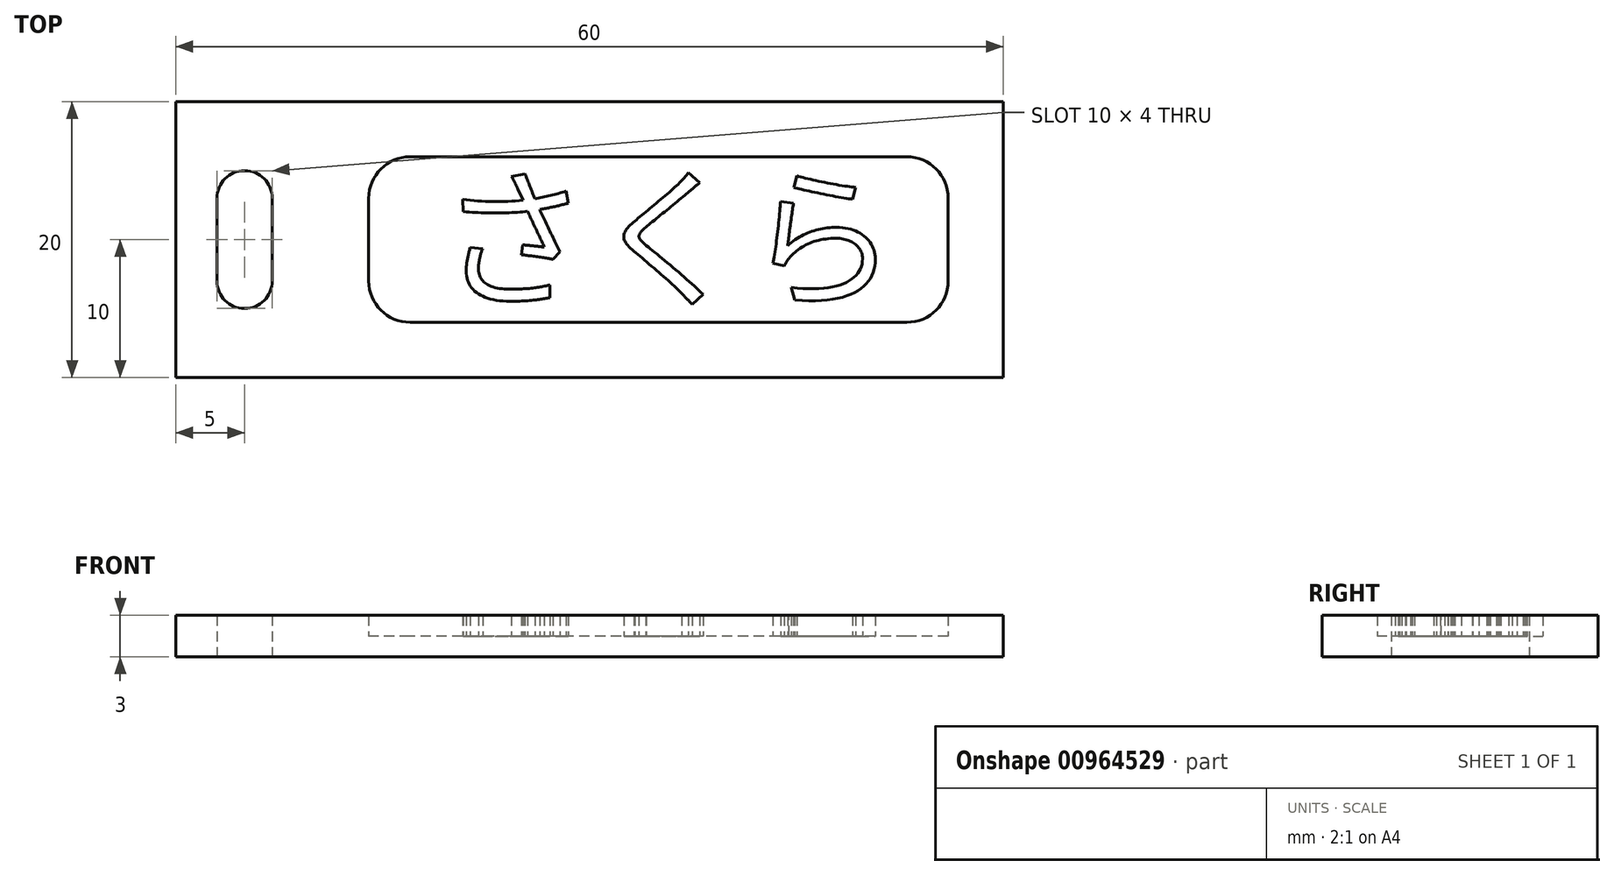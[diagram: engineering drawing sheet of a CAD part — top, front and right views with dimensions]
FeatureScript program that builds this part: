
annotation { "Feature Type Name" : "Feature", "Feature Type Description" : "" }
export const myFeature = defineFeature(function(context is Context, id is Id, definition is map)
    precondition{}
    {
        {
            var Q0;
            Q0=qCreatedBy(makeId("Top.planeOp"),FACE);
            var sketch = newSketch(context, id + "F0", { "sketchPlane" : qUnion([Q0])});
            skLineSegment(sketch, "E0.bottom", {"start": v(-25, 10) * mm, "end": v(25, 10) * mm});
            skLineSegment(sketch, "E0.top", {"start": v(-25, -10) * mm, "end": v(25, -10) * mm});
            skLineSegment(sketch, "E0.left", {"start": v(-25, 10) * mm, "end": v(-25, -10) * mm});
            skLineSegment(sketch, "E0.right", {"start": v(25, 10) * mm, "end": v(25, -10) * mm});
            skPoint(sketch, "E0.middle", {"position": v(0, 0) * mm});
            skLineSegment(sketch, "E1.bottom", {"start": v(-25, 0) * mm, "end": v(25, 0) * mm});
            skLineSegment(sketch, "E1.top", {"start": v(-25, 0) * mm, "end": v(25, 0) * mm});
            skLineSegment(sketch, "E1.left", {"start": v(-25, 0) * mm, "end": v(-25, 0) * mm});
            skLineSegment(sketch, "E1.right", {"start": v(25, 0) * mm, "end": v(25, 0) * mm});
            skLineSegment(sketch, "E2.bottom", {"start": v(-25, -10) * mm, "end": v(-35, -10) * mm});
            skLineSegment(sketch, "E2.top", {"start": v(-25, 10) * mm, "end": v(-35, 10) * mm});
            skLineSegment(sketch, "E2.left", {"start": v(-25, -10) * mm, "end": v(-25, 10) * mm});
            skLineSegment(sketch, "E2.right", {"start": v(-35, -10) * mm, "end": v(-35, 10) * mm});
            skPoint(sketch, "E2.middle", {"position": v(-30, 0) * mm});
            skLineSegment(sketch, "E3.bottom", {"start": v(-30, 5) * mm, "end": v(-30, 5) * mm});
            skLineSegment(sketch, "E3.top", {"start": v(-30, -5) * mm, "end": v(-30, -5) * mm});
            skLineSegment(sketch, "E3.left", {"start": v(-28, 3) * mm, "end": v(-28, -3) * mm});
            skLineSegment(sketch, "E3.right", {"start": v(-32, 3) * mm, "end": v(-32, -3) * mm});
            skPoint(sketch, "E4.visualSharp", {"position": v(-32, 5) * mm});
            skArc(sketch, "E4.filletArc", {"start": v(-30, 5) * mm, "mid": v(-31.41, 4.41) * mm, "end": v(-32, 3) * mm});
            skPoint(sketch, "E5.visualSharp", {"position": v(-28, 5) * mm});
            skArc(sketch, "E5.filletArc", {"start": v(-28, 3) * mm, "mid": v(-28.59, 4.41) * mm, "end": v(-30, 5) * mm});
            skPoint(sketch, "E6.visualSharp", {"position": v(-32, -5) * mm});
            skArc(sketch, "E6.filletArc", {"start": v(-32, -3) * mm, "mid": v(-31.41, -4.41) * mm, "end": v(-30, -5) * mm});
            skPoint(sketch, "E7.visualSharp", {"position": v(-28, -5) * mm});
            skArc(sketch, "E7.filletArc", {"start": v(-30, -5) * mm, "mid": v(-28.59, -4.41) * mm, "end": v(-28, -3) * mm});
            skSolve(sketch);
        }
        {
            var Q0;
            Q0 = qSketchRegion(id + "F0", true);
            extrude(context, id + "F1", {"entities" : qUnion([Q0]), "depth" : 3 * mm, "offsetDistance" : 25 * mm});
        }
        {
            var Q0;
            Q0=qCreatedBy(makeId("Top.planeOp"),FACE);
            var sketch = newSketch(context, id + "F2", { "sketchPlane" : qUnion([Q0])});
            skLineSegment(sketch, "E8.bottom", {"start": v(18, -6) * mm, "end": v(-18, -6) * mm});
            skLineSegment(sketch, "E8.top", {"start": v(18, 6) * mm, "end": v(-18, 6) * mm});
            skLineSegment(sketch, "E8.left", {"start": v(21, -3) * mm, "end": v(21, 3) * mm});
            skLineSegment(sketch, "E8.right", {"start": v(-21, -3) * mm, "end": v(-21, 3) * mm});
            skPoint(sketch, "E8.middle", {"position": v(0, 0) * mm});
            skPoint(sketch, "E9.visualSharp", {"position": v(-21, 6) * mm});
            skArc(sketch, "E9.filletArc", {"start": v(-18, 6) * mm, "mid": v(-20.12, 5.12) * mm, "end": v(-21, 3) * mm});
            skPoint(sketch, "E10.visualSharp", {"position": v(21, 6) * mm});
            skArc(sketch, "E10.filletArc", {"start": v(21, 3) * mm, "mid": v(20.12, 5.12) * mm, "end": v(18, 6) * mm});
            skPoint(sketch, "E11.visualSharp", {"position": v(21, -6) * mm});
            skArc(sketch, "E11.filletArc", {"start": v(18, -6) * mm, "mid": v(20.12, -5.12) * mm, "end": v(21, -3) * mm});
            skPoint(sketch, "E12.visualSharp", {"position": v(-21, -6) * mm});
            skArc(sketch, "E12.filletArc", {"start": v(-21, -3) * mm, "mid": v(-20.12, -5.12) * mm, "end": v(-18, -6) * mm});
            skSolve(sketch);
        }
        {
            var Q0;
            Q0 = qSketchRegion(id + "F2", true);
            extrude(context, id + "F3", {"entities" : qUnion([Q0]), "depth" : 3 * mm, "offsetDistance" : 25 * mm});
        }
        {
            var Q0;
            Q0=makeQuery(id+"F3.opExtrude","SWEPT_BODY",BODY,{"disambiguationData":[OSD([sQuery(id+"F2.wireOp",EDGE,"E8.bottom"),sQuery(id+"F2.wireOp",EDGE,"E8.top"),sQuery(id+"F2.wireOp",EDGE,"E8.left"),sQuery(id+"F2.wireOp",EDGE,"E8.right"),sQuery(id+"F2.wireOp",EDGE,"E9.filletArc"),sQuery(id+"F2.wireOp",EDGE,"E10.filletArc"),sQuery(id+"F2.wireOp",EDGE,"E11.filletArc"),sQuery(id+"F2.wireOp",EDGE,"E12.filletArc")])]});
            transform(context, id + "F4", {"entities" : qUnion([Q0]), "transformType" : TransformType.TRANSLATION_3D, "dx" : 0 * mm, "dy" : 0 * mm, "dz" : 1.5 * mm, "makeCopy" : false});
        }
        {
            var Q0;
            Q0=makeQuery(id+"F3.opExtrude","SWEPT_BODY",BODY,{"disambiguationData":[OSD([sQuery(id+"F2.wireOp",EDGE,"E8.bottom"),sQuery(id+"F2.wireOp",EDGE,"E8.top"),sQuery(id+"F2.wireOp",EDGE,"E8.left"),sQuery(id+"F2.wireOp",EDGE,"E8.right"),sQuery(id+"F2.wireOp",EDGE,"E9.filletArc"),sQuery(id+"F2.wireOp",EDGE,"E10.filletArc"),sQuery(id+"F2.wireOp",EDGE,"E11.filletArc"),sQuery(id+"F2.wireOp",EDGE,"E12.filletArc")])]});
            var Q1;
            Q1=makeQuery(id+"F1.opExtrude","SWEPT_BODY",BODY,{"disambiguationData":[OSD([sQuery(id+"F0.wireOp",EDGE,"E0.bottom"),sQuery(id+"F0.wireOp",EDGE,"E0.top"),sQuery(id+"F0.wireOp",EDGE,"E0.right"),sQuery(id+"F0.wireOp",EDGE,"E2.bottom"),sQuery(id+"F0.wireOp",EDGE,"E2.top"),sQuery(id+"F0.wireOp",EDGE,"E2.right"),sQuery(id+"F0.wireOp",EDGE,"E3.left"),sQuery(id+"F0.wireOp",EDGE,"E3.right"),sQuery(id+"F0.wireOp",EDGE,"E4.filletArc"),sQuery(id+"F0.wireOp",EDGE,"E5.filletArc"),sQuery(id+"F0.wireOp",EDGE,"E6.filletArc"),sQuery(id+"F0.wireOp",EDGE,"E7.filletArc")])]});
            booleanBodies(context, id + "F5", {"operationType" : BooleanOperationType.SUBTRACTION, "tools" : qUnion([Q0]), "targets" : qUnion([Q1])});
        }
        {
            var Q0;
            Q0=qCreatedBy(makeId("Top.planeOp"),FACE);
            var sketch = newSketch(context, id + "F6", { "sketchPlane" : qUnion([Q0])});
            skText(sketch, "E13", { "text": "さくら", "fontName": "NotoSansCJKjp-Regular.otf"});
            const initialGuessF6  = {"E13": [-0.01593, -0.00405, 1, 0, 0.008]};
            skSetInitialGuess(sketch, initialGuessF6);
            skSolve(sketch);
        }
        {
            var Q0;
            Q0 = qSketchRegion(id + "F6", true);
            extrude(context, id + "F7", {"entities" : qUnion([Q0]), "operationType" : NewBodyOperationType.ADD, "depth" : 3 * mm, "offsetDistance" : 25 * mm});
        }
    });
